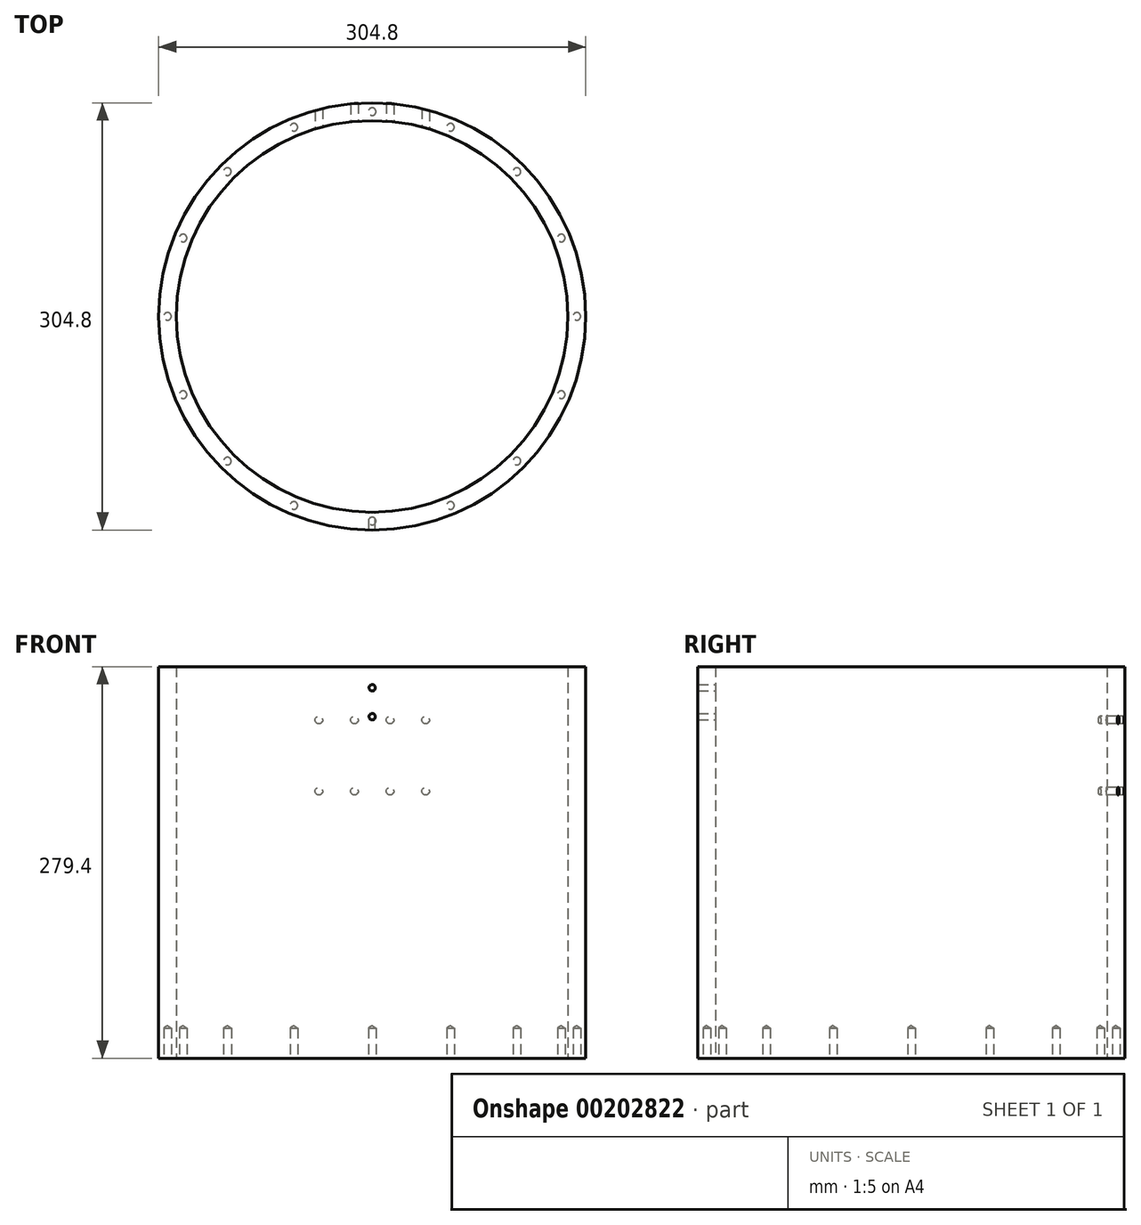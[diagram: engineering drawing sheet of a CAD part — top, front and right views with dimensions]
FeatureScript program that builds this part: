
annotation { "Feature Type Name" : "Feature", "Feature Type Description" : "" }
export const myFeature = defineFeature(function(context is Context, id is Id, definition is map)
    precondition{}
    {
        {
            var Q0;
            Q0=qCreatedBy(makeId("Top.planeOp"),FACE);
            var sketch = newSketch(context, id + "F0", { "sketchPlane" : qUnion([Q0])});
            skCircle(sketch, "E0", {"center": v(0, 0) * mm, "radius": 139.7 * mm});
            skCircle(sketch, "E1.0", {"center": v(0, 0) * mm, "radius": 152.4 * mm});
            skSolve(sketch);
        }
        {
            var Q0;
            Q0=makeQuery(id+"F0.imprint","IMPRINT",FACE,{"disambiguationData":[TD([[makeQuery(id+"F0.imprint","IMPRINT",EDGE,{"derivedFrom":sQuery(id+"F0.wireOp",EDGE,"E0")}),-1.0]])]});
            extrude(context, id + "F1", {"entities" : qUnion([Q0]), "depth" : 279.4 * mm});
        }
        {
            var Q0;
            Q0=makeQuery(id+"F1.opExtrude","CAP_FACE",FACE,{"disambiguationData":[OSD([sQuery(id+"F0.wireOp",EDGE,"E0"),sQuery(id+"F0.wireOp",EDGE,"E1.0")])],"isStart":true});
            var sketch = newSketch(context, id + "F2", { "sketchPlane" : qUnion([Q0])});
            skCircle(sketch, "E2", {"center": v(0, 0) * mm, "radius": 146.05 * mm, "construction": true});
            skPoint(sketch, "E3", {"position": v(-146.05, 0) * mm});
            skPoint(sketch, "E4.1.0", {"position": v(-134.93, -55.9) * mm});
            skPoint(sketch, "E4.2.0", {"position": v(-103.27, -103.27) * mm});
            skPoint(sketch, "E4.3.0", {"position": v(-55.9, -134.93) * mm});
            skPoint(sketch, "E4.4.0", {"position": v(0, -146.05) * mm});
            skPoint(sketch, "E4.5.0", {"position": v(55.9, -134.93) * mm});
            skPoint(sketch, "E4.6.0", {"position": v(103.27, -103.27) * mm});
            skPoint(sketch, "E4.7.0", {"position": v(134.93, -55.9) * mm});
            skPoint(sketch, "E4.8.0", {"position": v(146.05, 0) * mm});
            skPoint(sketch, "E4.9.0", {"position": v(134.93, 55.9) * mm});
            skPoint(sketch, "E4.10.0", {"position": v(103.27, 103.27) * mm});
            skPoint(sketch, "E4.11.0", {"position": v(55.9, 134.93) * mm});
            skPoint(sketch, "E5.0.12.0", {"position": v(0, 146.05) * mm});
            skPoint(sketch, "E5.0.13.0", {"position": v(-55.9, 134.93) * mm});
            skPoint(sketch, "E5.0.14.0", {"position": v(-103.27, 103.27) * mm});
            skPoint(sketch, "E5.0.15.0", {"position": v(-134.93, 55.9) * mm});
            skSolve(sketch);
        }
        {
            var Q0;
            Q0=sQuery(id+"F2.wireOp",VERTEX,"E5.0.15.0");
            var Q1;
            Q1=sQuery(id+"F2.wireOp",VERTEX,"E5.0.14.0");
            var Q2;
            Q2=sQuery(id+"F2.wireOp",VERTEX,"E5.0.13.0");
            var Q3;
            Q3=sQuery(id+"F2.wireOp",VERTEX,"E5.0.12.0");
            var Q4;
            Q4=sQuery(id+"F2.wireOp",VERTEX,"E4.11.0");
            var Q5;
            Q5=sQuery(id+"F2.wireOp",VERTEX,"E4.10.0");
            var Q6;
            Q6=sQuery(id+"F2.wireOp",VERTEX,"E4.9.0");
            var Q7;
            Q7=sQuery(id+"F2.wireOp",VERTEX,"E4.8.0");
            var Q8;
            Q8=sQuery(id+"F2.wireOp",VERTEX,"E4.7.0");
            var Q9;
            Q9=sQuery(id+"F2.wireOp",VERTEX,"E4.6.0");
            var Q10;
            Q10=sQuery(id+"F2.wireOp",VERTEX,"E4.5.0");
            var Q11;
            Q11=sQuery(id+"F2.wireOp",VERTEX,"E4.4.0");
            var Q12;
            Q12=sQuery(id+"F2.wireOp",VERTEX,"E4.3.0");
            var Q13;
            Q13=sQuery(id+"F2.wireOp",VERTEX,"E4.2.0");
            var Q14;
            Q14=sQuery(id+"F2.wireOp",VERTEX,"E4.1.0");
            var Q15;
            Q15=sQuery(id+"F2.wireOp",VERTEX,"E3");
            var Q16;
            Q16=makeQuery(id+"F1.opExtrude","SWEPT_BODY",BODY,{"disambiguationData":[OSD([sQuery(id+"F0.wireOp",EDGE,"E0"),sQuery(id+"F0.wireOp",EDGE,"E1.0")])]});
            hole(context, id + "F3", {"style" : HoleStyle.SIMPLE, "endStyle" : HoleEndStyle.BLIND, "standardTappedOrClearance" : lookupTablePath({ "standard" : "ANSI", "engagement" : "75%", "pitch" : "28 tpi", "size" : "1/4", "type" : "Tapped" }), "standardBlindInLast" : lookupTablePath({ "standard" : "ANSI", "engagement" : "75%", "pitch" : "28 tpi", "size" : "1/4", "type" : "Tapped" }), "holeDiameter" : 5.4 * mm, "holeDepth" : 21.59 * mm, "startFromSketch" : true, "locations" : qUnion([Q0, Q1, Q2, Q3, Q4, Q5, Q6, Q7, Q8, Q9, Q10, Q11, Q12, Q13, Q14, Q15]), "scope" : qUnion([Q16]), "majorDiameter" : 6.35 * mm});
        }
        {
            var Q0;
            Q0=qCreatedBy(makeId("Front.planeOp"),FACE);
            var sketch = newSketch(context, id + "F4", { "sketchPlane" : qUnion([Q0])});
            skLineSegment(sketch, "E6.0", {"start": v(-152.4, 279.4) * mm, "end": v(152.4, 279.4) * mm});
            skLineSegment(sketch, "E7", {"start": v(0, 0) * mm, "end": v(0, 279.4) * mm, "construction": true});
            skPoint(sketch, "E8", {"position": v(0, 264.32) * mm});
            skPoint(sketch, "E9", {"position": v(0, 243.68) * mm});
            skPoint(sketch, "E10", {"position": v(12.7, 241.3) * mm});
            skPoint(sketch, "E11.0.1.0", {"position": v(12.7, 190.5) * mm});
            skPoint(sketch, "E11.1.0.0", {"position": v(38.1, 241.3) * mm});
            skPoint(sketch, "E11.1.1.0", {"position": v(38.1, 190.5) * mm});
            skLineSegment(sketch, "E11.direction1", {"start": v(12.7, 241.3) * mm, "end": v(38.1, 241.3) * mm, "construction": true});
            skLineSegment(sketch, "E11.direction2", {"start": v(12.7, 241.3) * mm, "end": v(12.7, 190.5) * mm, "construction": true});
            skPoint(sketch, "E12.1.0.0", {"position": v(-12.7, 241.3) * mm});
            skPoint(sketch, "E12.1.1.0", {"position": v(-12.7, 190.5) * mm});
            skPoint(sketch, "E12.2.0.0", {"position": v(-38.1, 241.3) * mm});
            skPoint(sketch, "E12.2.1.0", {"position": v(-38.1, 190.5) * mm});
            skLineSegment(sketch, "E12.direction1", {"start": v(12.7, 241.3) * mm, "end": v(-12.7, 241.3) * mm, "construction": true});
            skSolve(sketch);
        }
        {
            var Q0;
            Q0=sQuery(id+"F4.wireOp",VERTEX,"E8");
            var Q1;
            Q1=sQuery(id+"F4.wireOp",VERTEX,"E9");
            var Q2;
            Q2=makeQuery(id+"F1.opExtrude","SWEPT_BODY",BODY,{"disambiguationData":[OSD([sQuery(id+"F0.wireOp",EDGE,"E0"),sQuery(id+"F0.wireOp",EDGE,"E1.0")])]});
            hole(context, id + "F5", {"style" : HoleStyle.SIMPLE, "endStyle" : HoleEndStyle.THROUGH, "oppositeDirection" : true, "holeDiameter" : 4.5 * mm, "startFromSketch" : true, "locations" : qUnion([Q0, Q1]), "scope" : qUnion([Q2]), "isTappedThrough" : true});
        }
        {
            var Q0;
            Q0=sQuery(id+"F4.wireOp",VERTEX,"E11.1.0.0");
            var Q1;
            Q1=sQuery(id+"F4.wireOp",VERTEX,"E10");
            var Q2;
            Q2=sQuery(id+"F4.wireOp",VERTEX,"E11.1.1.0");
            var Q3;
            Q3=sQuery(id+"F4.wireOp",VERTEX,"E11.0.1.0");
            var Q4;
            Q4=sQuery(id+"F4.wireOp",VERTEX,"E12.1.1.0");
            var Q5;
            Q5=sQuery(id+"F4.wireOp",VERTEX,"E12.1.0.0");
            var Q6;
            Q6=sQuery(id+"F4.wireOp",VERTEX,"E12.2.0.0");
            var Q7;
            Q7=sQuery(id+"F4.wireOp",VERTEX,"E12.2.1.0");
            var Q8;
            Q8=makeQuery(id+"F1.opExtrude","SWEPT_BODY",BODY,{"disambiguationData":[OSD([sQuery(id+"F0.wireOp",EDGE,"E0"),sQuery(id+"F0.wireOp",EDGE,"E1.0")])]});
            hole(context, id + "F6", {"style" : HoleStyle.SIMPLE, "endStyle" : HoleEndStyle.THROUGH, "standardTappedOrClearance" : lookupTablePath({ "standard" : "ANSI", "engagement" : "75%", "pitch" : "28 tpi", "size" : "1/4", "type" : "Tapped" }), "standardBlindInLast" : lookupTablePath({ "standard" : "ANSI", "engagement" : "75%", "pitch" : "28 tpi", "size" : "1/4", "type" : "Tapped" }), "holeDiameter" : 5.4 * mm, "startFromSketch" : true, "locations" : qUnion([Q0, Q1, Q2, Q3, Q4, Q5, Q6, Q7]), "scope" : qUnion([Q8]), "isTappedThrough" : true, "majorDiameter" : 6.35 * mm, "showTappedDepth" : true});
        }
    });
